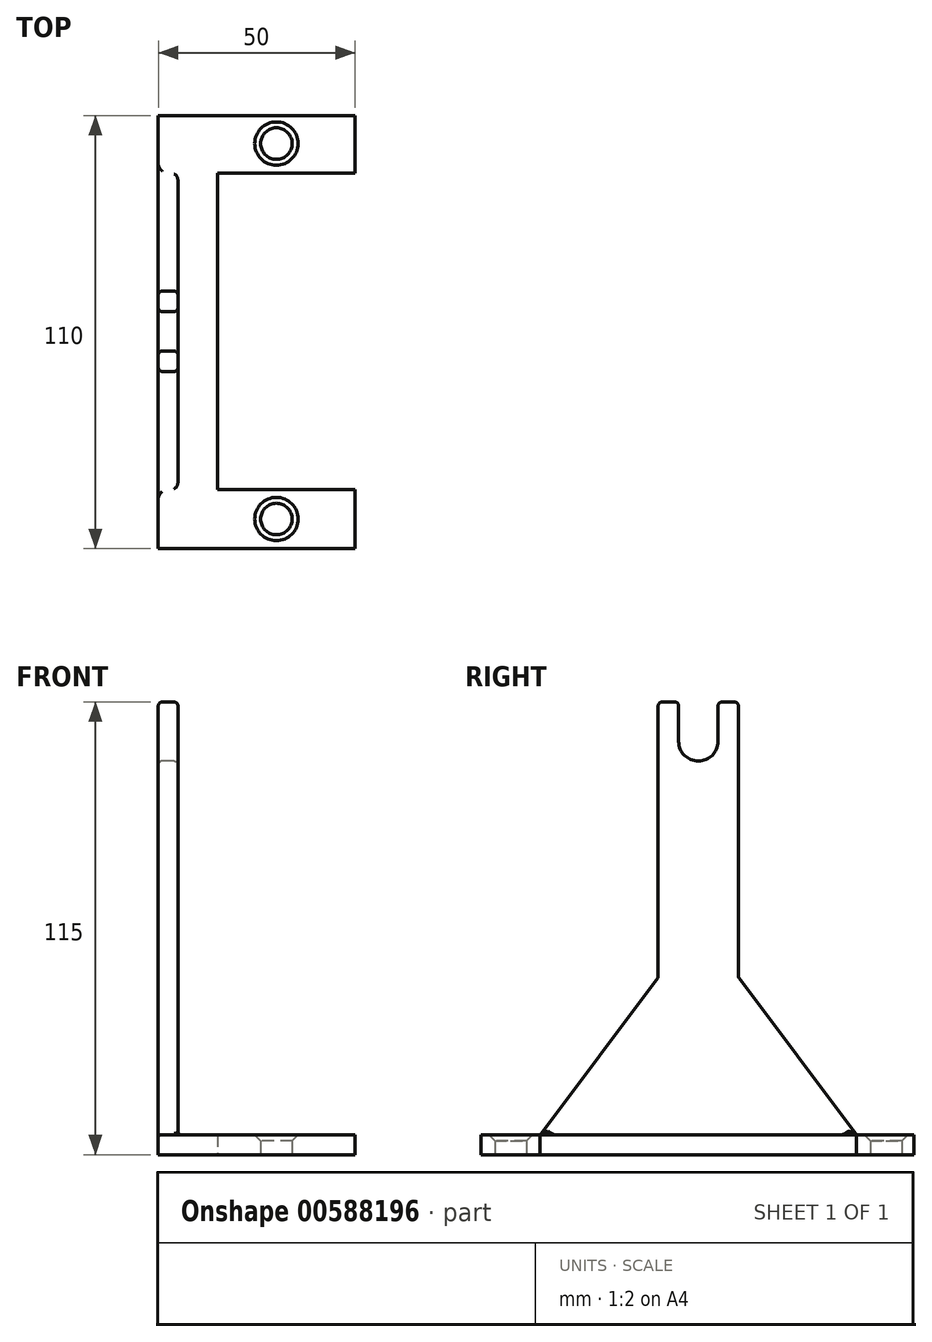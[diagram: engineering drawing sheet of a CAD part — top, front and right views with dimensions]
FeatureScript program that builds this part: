
annotation { "Feature Type Name" : "Feature", "Feature Type Description" : "" }
export const myFeature = defineFeature(function(context is Context, id is Id, definition is map)
    precondition{}
    {
        {
            var Q0;
            Q0=qCreatedBy(makeId("Top.planeOp"),FACE);
            var sketch = newSketch(context, id + "F0", { "sketchPlane" : qUnion([Q0])});
            skLineSegment(sketch, "E0.bottom", {"start": v(-56.8, 35.23) * mm, "end": v(-6.8, 35.23) * mm});
            skLineSegment(sketch, "E0.top", {"start": v(-56.8, -74.77) * mm, "end": v(-6.8, -74.77) * mm});
            skLineSegment(sketch, "E0.left", {"start": v(-56.8, 35.23) * mm, "end": v(-56.8, -74.77) * mm});
            skLineSegment(sketch, "E0.right", {"start": v(-6.8, 35.23) * mm, "end": v(-6.8, 20.62) * mm});
            skLineSegment(sketch, "E1.0", {"start": v(-41.8, -59.77) * mm, "end": v(-6.8, -59.77) * mm});
            skLineSegment(sketch, "E2.0", {"start": v(-57.53, 35.62) * mm, "end": v(-7.53, 35.62) * mm});
            skLineSegment(sketch, "E3.0", {"start": v(-41.8, 20.62) * mm, "end": v(-6.8, 20.62) * mm});
            skLineSegment(sketch, "E4.0", {"start": v(-41.8, 20.62) * mm, "end": v(-41.8, -59.77) * mm});
            skLineSegment(sketch, "E5.trimOffspring", {"start": v(-6.8, -59.77) * mm, "end": v(-6.8, -74.77) * mm});
            skLineSegment(sketch, "E6.0", {"start": v(-42.53, -67.27) * mm, "end": v(-7.53, -67.27) * mm, "construction": true});
            skLineSegment(sketch, "E7.0", {"start": v(-42.53, 28.12) * mm, "end": v(-7.53, 28.12) * mm, "construction": true});
            skLineSegment(sketch, "E8.0", {"start": v(-26.8, -59.77) * mm, "end": v(-26.8, -74.77) * mm, "construction": true});
            skLineSegment(sketch, "E9.0", {"start": v(-26.8, 35.23) * mm, "end": v(-26.8, 20.62) * mm, "construction": true});
            skCircle(sketch, "E10", {"center": v(-26.8, -67.27) * mm, "radius": 4 * mm});
            skCircle(sketch, "E11", {"center": v(-26.8, 28.12) * mm, "radius": 4 * mm});
            skSolve(sketch);
        }
        {
            var Q0;
            Q0=makeQuery(id+"F0.imprint","IMPRINT",FACE,{"disambiguationData":[TD([[makeQuery(id+"F0.imprint","IMPRINT",EDGE,{"derivedFrom":sQuery(id+"F0.wireOp",EDGE,"E0.bottom")}),-1.0]])]});
            extrude(context, id + "F1", {"entities" : qUnion([Q0]), "depth" : 5 * mm, "offsetDistance" : 25 * mm});
        }
        {
            var Q0;
            Q0=makeQuery(id+"F1.opExtrude","CAP_FACE",FACE,{"disambiguationData":[OSD([sQuery(id+"F0.wireOp",EDGE,"E0.bottom"),sQuery(id+"F0.wireOp",EDGE,"E0.top"),sQuery(id+"F0.wireOp",EDGE,"E0.left"),sQuery(id+"F0.wireOp",EDGE,"E0.right"),sQuery(id+"F0.wireOp",EDGE,"E1.0"),sQuery(id+"F0.wireOp",EDGE,"E3.0"),sQuery(id+"F0.wireOp",EDGE,"E4.0"),sQuery(id+"F0.wireOp",EDGE,"E5.trimOffspring"),sQuery(id+"F0.wireOp",EDGE,"E10"),sQuery(id+"F0.wireOp",EDGE,"E11")])],"isStart":false});
            var sketch = newSketch(context, id + "F2", { "sketchPlane" : qUnion([Q0])});
            skLineSegment(sketch, "E12", {"start": v(-51.8, -59.77) * mm, "end": v(-56.8, -59.77) * mm});
            skLineSegment(sketch, "E13", {"start": v(-51.8, 20.62) * mm, "end": v(-56.8, 20.62) * mm});
            skLineSegment(sketch, "E14.0", {"start": v(-51.8, 20.62) * mm, "end": v(-51.8, -59.77) * mm});
            skSolve(sketch);
        }
        {
            var Q0;
            {var subQ0=sQuery(id+"F2.wireOp",EDGE,"E12");Q0=makeQuery(id+"F2.imprint","IMPRINT",FACE,{"disambiguationData":[TD([[makeQuery(id+"F2.imprint","IMPRINT",EDGE,{"derivedFrom":subQ0}),-1.0]])]});}
            extrude(context, id + "F3", {"entities" : qUnion([Q0]), "operationType" : NewBodyOperationType.ADD, "depth" : 110 * mm, "offsetDistance" : 25 * mm});
        }
        {
            var Q0;
            {var subQ0=sQuery(id+"F0.wireOp",EDGE,"E0.left");Q0=makeQuery(id+"F3.boolean.opBoolean","MERGE",FACE,{"derivedFrom":[makeQuery(id+"F1.opExtrude","SWEPT_FACE",FACE,{"disambiguationData":[OSD([subQ0])]}),makeQuery(id+"F3.opExtrude","SWEPT_FACE",FACE,{"disambiguationData":[OSD([subQ0])]})]});}
            var sketch = newSketch(context, id + "F4", { "sketchPlane" : qUnion([Q0])});
            skLineSegment(sketch, "E15.0", {"start": v(9.38, 115) * mm, "end": v(9.38, 5) * mm, "construction": true});
            skLineSegment(sketch, "E16.0", {"start": v(29.77, 115) * mm, "end": v(29.77, 5) * mm, "construction": true});
            skLineSegment(sketch, "E17.0", {"start": v(-20.62, 45) * mm, "end": v(9.38, 45) * mm, "construction": true});
            skLineSegment(sketch, "E18", {"start": v(9.38, 45) * mm, "end": v(-20.62, 5) * mm});
            skLineSegment(sketch, "E19", {"start": v(29.77, 45) * mm, "end": v(59.77, 5) * mm});
            skLineSegment(sketch, "E20", {"start": v(9.38, 45) * mm, "end": v(9.38, 115) * mm});
            skLineSegment(sketch, "E21", {"start": v(29.77, 45) * mm, "end": v(29.77, 115) * mm});
            skLineSegment(sketch, "E22.trimOffspring", {"start": v(29.77, 45) * mm, "end": v(59.77, 45) * mm, "construction": true});
            skLineSegment(sketch, "E23.0", {"start": v(-20.62, 105) * mm, "end": v(59.77, 105) * mm, "construction": true});
            skLineSegment(sketch, "E24", {"start": v(19.58, 115) * mm, "end": v(19.58, 105) * mm, "construction": true});
            skArc(sketch, "E25", {"start": v(14.58, 105) * mm, "mid": v(19.58, 100) * mm, "end": v(24.58, 105) * mm});
            skLineSegment(sketch, "E26", {"start": v(24.58, 105) * mm, "end": v(24.58, 115) * mm});
            skLineSegment(sketch, "E27", {"start": v(14.58, 105) * mm, "end": v(14.58, 115) * mm});
            skSolve(sketch);
        }
        {
            var Q0;
            Q0=makeQuery(id+"F4.imprint","IMPRINT",FACE,{"disambiguationData":[TD([[makeQuery(id+"F4.imprint","IMPRINT",EDGE,{"derivedFrom":sQuery(id+"F4.wireOp",EDGE,"E18")}),-1.0]])]});
            var Q1;
            Q1=makeQuery(id+"F4.imprint","IMPRINT",FACE,{"disambiguationData":[TD([[makeQuery(id+"F4.imprint","IMPRINT",EDGE,{"derivedFrom":sQuery(id+"F4.wireOp",EDGE,"E19")}),1.0]])]});
            var Q2;
            Q2=makeQuery(id+"F4.imprint","IMPRINT",FACE,{"disambiguationData":[TD([[makeQuery(id+"F4.imprint","IMPRINT",EDGE,{"derivedFrom":sQuery(id+"F4.wireOp",EDGE,"E25")}),1.0]])]});
            extrude(context, id + "F5", {"entities" : qUnion([Q0, Q1, Q2]), "operationType" : NewBodyOperationType.REMOVE, "oppositeDirection" : true, "depth" : 25 * mm, "offsetDistance" : 25 * mm});
        }
        {
            var Q0;
            Q0=makeQuery(id+"F1.opExtrude","CAP_EDGE",EDGE,{"disambiguationData":[OSD([sQuery(id+"F0.wireOp",EDGE,"E10")])],"isStart":false});
            var Q1;
            Q1=makeQuery(id+"F1.opExtrude","CAP_EDGE",EDGE,{"disambiguationData":[OSD([sQuery(id+"F0.wireOp",EDGE,"E11")])],"isStart":false});
            chamfer(context, id + "F6", {"entities" : qUnion([Q0, Q1]), "width" : 1.5 * mm, "tangentPropagation" : true});
        }
        {
            var Q0;
            Q0=makeQuery(id+"F5.boolean.opBoolean","INTERSECT",EDGE,{"derivedFrom":[makeQuery(id+"F3.opExtrude","SWEPT_FACE",FACE,{"disambiguationData":[OSD([sQuery(id+"F2.wireOp",EDGE,"E14.0")])]}),makeQuery(id+"F5.opExtrude","SWEPT_FACE",FACE,{"disambiguationData":[OSD([sQuery(id+"F4.wireOp",EDGE,"E20")])]})]});
            var Q1;
            Q1=makeQuery(id+"F5.boolean.opBoolean","COPY",FACE,{"derivedFrom":makeQuery(id+"F5.opExtrude","SWEPT_FACE",FACE,{"disambiguationData":[OSD([sQuery(id+"F4.wireOp",EDGE,"E19")])]})});
            var Q2;
            Q2=makeQuery(id+"F5.boolean.opBoolean","COPY",FACE,{"derivedFrom":makeQuery(id+"F5.opExtrude","SWEPT_FACE",FACE,{"disambiguationData":[OSD([sQuery(id+"F4.wireOp",EDGE,"E21")])]})});
            var Q3;
            {var subQ0=sQuery(id+"F0.wireOp",EDGE,"E0.left");var subQ1=sQuery(id+"F2.wireOp",EDGE,"E14.0");Q3=makeQuery(id+"F5.boolean.opBoolean","SPLIT",FACE,{"disambiguationData":[TD([makeQuery(id+"F5.opExtrude","SWEPT_FACE",FACE,{"disambiguationData":[OSD([sQuery(id+"F4.wireOp",EDGE,"E21")])]})])],"derivedFrom":makeQuery(id+"F3.opExtrude","CAP_FACE",FACE,{"disambiguationData":[OSD([subQ0,sQuery(id+"F2.wireOp",EDGE,"E12"),sQuery(id+"F2.wireOp",EDGE,"E13"),subQ1])],"isStart":false})});}
            var Q4;
            {var subQ0=sQuery(id+"F0.wireOp",EDGE,"E0.left");var subQ1=sQuery(id+"F2.wireOp",EDGE,"E14.0");Q4=makeQuery(id+"F5.boolean.opBoolean","SPLIT",FACE,{"disambiguationData":[TD([makeQuery(id+"F5.opExtrude","SWEPT_FACE",FACE,{"disambiguationData":[OSD([sQuery(id+"F4.wireOp",EDGE,"E20")])]})])],"derivedFrom":makeQuery(id+"F3.opExtrude","CAP_FACE",FACE,{"disambiguationData":[OSD([subQ0,sQuery(id+"F2.wireOp",EDGE,"E12"),sQuery(id+"F2.wireOp",EDGE,"E13"),subQ1])],"isStart":false})});}
            var Q5;
            Q5=makeQuery(id+"F5.boolean.opBoolean","COPY",FACE,{"derivedFrom":makeQuery(id+"F5.opExtrude","SWEPT_FACE",FACE,{"disambiguationData":[OSD([sQuery(id+"F4.wireOp",EDGE,"E20")])]})});
            var Q6;
            Q6=makeQuery(id+"F5.boolean.opBoolean","COPY",FACE,{"derivedFrom":makeQuery(id+"F5.opExtrude","SWEPT_FACE",FACE,{"disambiguationData":[OSD([sQuery(id+"F4.wireOp",EDGE,"E18")])]})});
            var Q7;
            Q7=makeQuery(id+"F5.boolean.opBoolean","COPY",FACE,{"derivedFrom":makeQuery(id+"F5.opExtrude","SWEPT_FACE",FACE,{"disambiguationData":[OSD([sQuery(id+"F4.wireOp",EDGE,"E26")])]})});
            var Q8;
            Q8=makeQuery(id+"F5.boolean.opBoolean","COPY",FACE,{"derivedFrom":makeQuery(id+"F5.opExtrude","SWEPT_FACE",FACE,{"disambiguationData":[OSD([sQuery(id+"F4.wireOp",EDGE,"E25")])]})});
            var Q9;
            Q9=makeQuery(id+"F5.boolean.opBoolean","COPY",FACE,{"derivedFrom":makeQuery(id+"F5.opExtrude","SWEPT_FACE",FACE,{"disambiguationData":[OSD([sQuery(id+"F4.wireOp",EDGE,"E27")])]})});
            fillet(context, id + "F7", {"entities" : qUnion([Q0, Q1, Q2, Q3, Q4, Q5, Q6, Q7, Q8, Q9]), "radius" : 1 * mm, "tangentPropagation" : true, "allowEdgeOverflow" : false});
        }
    });
